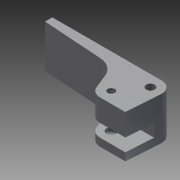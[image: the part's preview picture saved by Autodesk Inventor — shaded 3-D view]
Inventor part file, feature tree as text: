
AUTODESK INVENTOR PART (.ipt)
format: ipt  version: 2015 (Build 190159000, 159)  size: 175,616 bytes
history: native  units: mm
features: extrude x6, hole x6, chamfer x3
ambient origin geometry x8: Origin, YZ Plane, XZ Plane, XY Plane, X Axis, Y Axis, Z Axis, Center Point
bodies: Solid1 (feature_tree)
feature tree (15):
  extrude  "Extrusión1"  Depth=3.0mm
  extrude  "Extrusión7"  Depth=17.25mm
  hole  "Agujero5"  [1 undecoded]
  hole  "Agujero6"  [1 undecoded]
  extrude  "Extrusión8"  Depth=4.0mm
  extrude  "Extrusión9"  Depth=10.0mm TaperAngle=0.0deg
  chamfer  "Chaflán4"  Distance=1.0mm Angle=45.0deg
  hole  "Agujero1"  [1 undecoded]
  hole  "Agujero2"  [1 undecoded]
  hole  "Agujero3"  [1 undecoded]
  extrude  "Extrusión5"  Depth=42.5mm
  chamfer  "Chaflán1"  Distance=2.0mm
  extrude  "Extrusión6"  Depth=5.5mm
  hole  "Agujero4"  [1 undecoded]
  chamfer  "Chaflán2"  Distance=10.0mm
note: 6 required parameter values undecoded (feature->parameter linkage not recoverable at this tier; creation-order binding heuristic only, values carry confidence <= 0.55)
